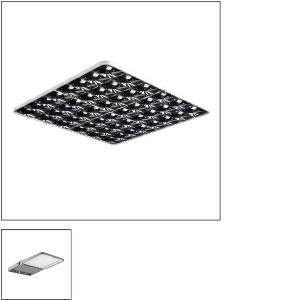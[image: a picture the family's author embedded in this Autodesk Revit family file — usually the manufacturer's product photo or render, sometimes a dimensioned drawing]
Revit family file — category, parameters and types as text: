
# Revit family: siteco_mirrortec_r__indoor___rs05_5nw14093qb_2604
name_source: partatom
category: Lighting Fixtures
units: mm (PartAtom-declared; Revit-internal decimal feet)

## family parameters
Cut with Voids When Loaded = No
Host = Face
Light Source = No
Part Type = Normal
Room Calculation Point = No
Round Connector Dimension = Use Diameter
Shared = No

## types (1)
- 5XA7682G2H2AC (1 x LED, 33820 lm, 305.7 W, 4000K)
    Apparent Load = 306 VA
    CIE Flux Codes = 47 83 98 55 100
    Color Rendering = 70
    Color Temperature = 4000K
    Default Elevation = 1800 mm
    Description = secondary reflector, for Siteco Mirrortec® Indoor, wire hanger, housing, square, of aluminium, coated, metallic grey (RAL 9006), fresnel reflector 100, of PMMA, aluminized, highly specular, light point resolution, fresnel structure, length: 900 mm, width: 900 mm

Light Distribution: RS05
    Height = 12 mm  [stored 0.0393701 ft]
    Lamp = 1 x LED
    Lamp Light Flux = 33820 lm
    Lamp Power = 305.7 W
    Lamp count = 1
    Length = 919 mm
    Luminous efficacy = 111 lm/W
    Manufacturer = Siteco
    ModVariant = No
    Model = 5NW14093QB
    Mounting Place = Ceiling
    Mounting Type = Pendant
    Number of Poles = 1
    OnlyDefault = Yes
    Power Factor = 1
    Product Name = Siteco Mirrortec® Indoor | RS05
    Product group = secondary reflector
    ProductGroupID = 910
    Protection Class = Protection class II
    Protection Degree = IP 66
    RLX_Detail_Level = 1
    RlxData = <blob elided: 103265 chars, md5=0d720e2e>
    Socket = socket
    Standby Power = 0 W
    System Light Flux = 33820 lm
    System Power = 306 W
    Type Comments = Floodlight FL 20 midi, floodlight, primary light control with lens, of plastic, primary optical cover: protective disc, of toughened safety glass, transparent, light distribution: RS05, light emission: direct distribution, primary light characteristic: rotationally symmetric, installation type: surface-mounted, LED High Power LED, rated luminous flux: 38.380 lm, light colour: 740, colour temperature: 4000K, control gear: ECG Plus, control: overheat protection, power reduction, digital communication interface, time-dependent luminous flux control, flexible luminous flux parameterisation, electronic power reduction, with terminal, 10-pole, max. 2.5mm², mains connection: 220..240V, AC, 50/60Hz, rated input power: 306W, LED unit, of diecast aluminium, powder-coated, Siteco® metallic grey (DB 702S), length: 731 mm, width: 450 mm, height: 76mm, housing frame, of diecast aluminium, powder-coated, Siteco® metallic grey (DB 702S), wall fastening, DALIprotection rating (complete): IP66, insulation class (complete): insulation class II (safety insulation), certification: CE, ENEC, VDE, protection symbol: D, permissible ambient temperature for indoor applications: -40..+40°C, permissible ambient temperature for outdoor applications: -40..+50°C, standard: DIN EN 12944, packaging unit: 1 piece

individual setting: distance floodlight mirror = 2,5m / reflector tilt = 5°
    Type Image = l_577132_1005944.jpg
    URL = http://relux.com
    VarID = 5xa7682g2h2ac@adj_128715
    Voltage = 0 V
    Weight = 0.00 kg
    Width = 919 mm

note: [stored X ft] marks values corroborated as IEEE doubles in the binary element streams (Revit-internal decimal feet)

## geometry (parser evidence)
native form markers: Blend x4, Sweep x9
no freeform markers — native parametric forms only
